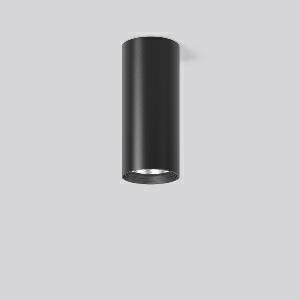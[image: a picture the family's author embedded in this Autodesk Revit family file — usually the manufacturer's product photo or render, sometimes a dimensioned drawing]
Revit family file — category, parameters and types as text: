
# Revit family: heledon_mini_a_931210_003_3_dea1
name_source: partatom
category: Lighting Fixtures
units: mm (PartAtom-declared; Revit-internal decimal feet)

## family parameters
Cut with Voids When Loaded = No
Host = Face
Light Source = No
Part Type = Normal
Room Calculation Point = No
Round Connector Dimension = Use Diameter
Shared = No

## types (1)
- HELEDON mini A (1 x LED Modul 935, 3800 lm, 3500)
    Apparent Load = 29 VA
    Approval mark = CE
    CIE Flux Codes = 95 99 100 100 100
    Color Rendering = 92
    Color Temperature = 3500
    Default Elevation = 1800 mm
    Description = Series: HELEDON mini
Cylindrical surface-mounted downlight. Housing: die-cast aluminium, powder-coated. Internal ceiling frame polycarbonate with bayonet mounting. Black plastic ring and recessed LED to prevent glare from the side. Optical assembly with reflector made of MIRO-Silver with 98% total light reflection for outstanding efficiency - can be changed without tools. Best colour rendering index Ra>90. Suitable for Ceiling mounting. Easy installation with a separate ceiling frame with bayonet mounting and plug connection. Driver integrated. Connected via plug-in connector. High quality converter without flickering and stroboscopic effect. The following accessories can be mounted without use of tools: interchangeable lenses, decorative glasses, honeycomb louvre, clear and frosted diffusers, white interchangeable plastic ring. 
Colour: deep black, matt (RAL 9005)
Diameter: 87 mm
Height: 197 mm
Lamp: LED
Socket: without socket
Colour temperature: 3500K
Colour rendering index (CRI): 92
System power: 29 W
Rated luminous flux: 3800 lm
Luminous efficiency: 131 lm/W
Control gear: Regulated power supply
Protection class: I
Type of protection: IP 20
    Height = 197 mm
    Lamp = 1 x LED Modul 935
    Lamp Light Flux = 3800 lm
    Lamp count = 1
    Length = 87 mm
    Lifetime = 50000 h
    Luminous efficacy = 131 lm/W
    Manufacturer = RZB
    ModVariant = No
    Model = 931210.003.3
    Mounting Place = Ceiling
    Mounting Type = Surface mounted
    Number of Poles = 1
    OnlyDefault = Yes
    Power Factor = 1
    Product Name = HELEDON mini A
    Product group = Surface mounted downlights
    ProductGroupID = 302
    Protection Class = Protection class I
    Protection Degree = IP 20
    RLX_Detail_Level = 1
    RLX_Emergency_Light_Flux = 0 lm
    RLX_Emergency_Type = 0
    RLX_Emergency_Type_DB = No
    RlxData = <blob elided: 106665 chars, md5=356568f1>
    Socket = socket
    Standby Power = 0 W
    System Light Flux = 3800 lm
    System Power = 29 W
    Type Comments = Product without accessories
    Type Image = 931188.003.jpg
    URL = http://relux.com
    VarID = ---
    Voltage = 230 V
    Voltage Range = 220-240 V
    Weight = 0.00 kg
    Width = 0 mm  [stored 0 ft]

note: [stored X ft] marks values corroborated as IEEE doubles in the binary element streams (Revit-internal decimal feet)

## geometry (parser evidence)
native form markers: Blend x4, Sweep x12
no freeform markers — native parametric forms only
